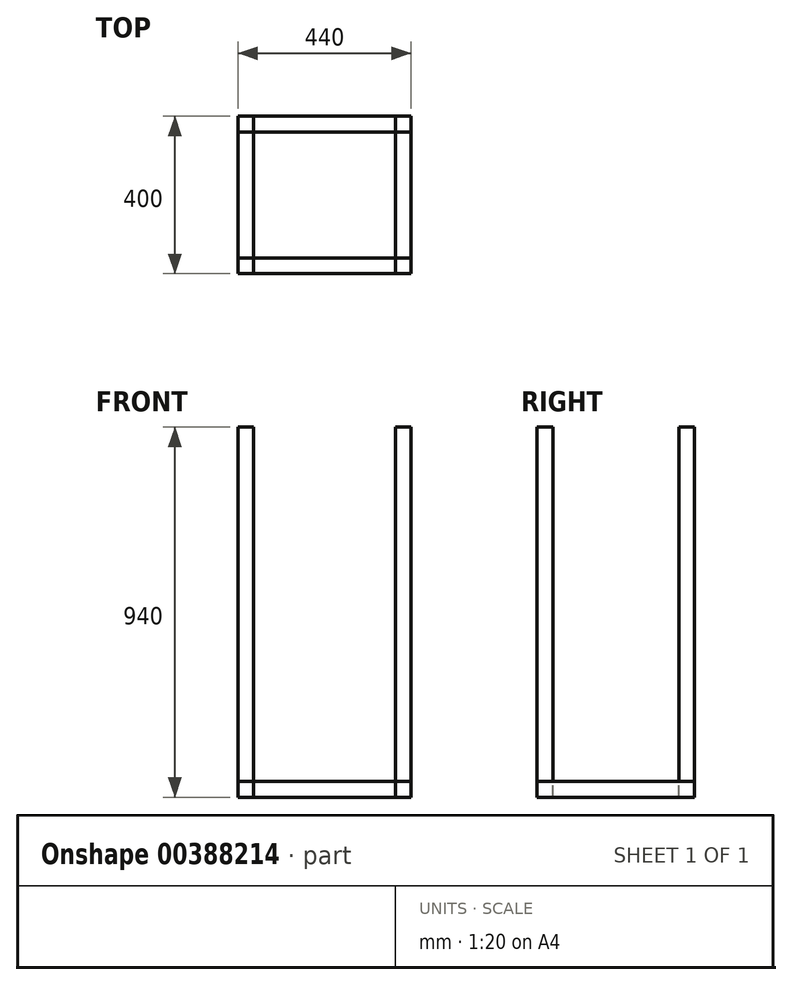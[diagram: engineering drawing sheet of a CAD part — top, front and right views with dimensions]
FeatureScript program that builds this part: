
annotation { "Feature Type Name" : "Feature", "Feature Type Description" : "" }
export const myFeature = defineFeature(function(context is Context, id is Id, definition is map)
    precondition{}
    {
        {
            var Q0;
            Q0=qCreatedBy(makeId("Top.planeOp"),FACE);
            var sketch = newSketch(context, id + "F0", { "sketchPlane" : qUnion([Q0])});
            skLineSegment(sketch, "E0.bottom", {"start": v(0, 0) * mm, "end": v(-40, 0) * mm});
            skLineSegment(sketch, "E0.top", {"start": v(0, 40) * mm, "end": v(-40, 40) * mm});
            skLineSegment(sketch, "E0.left", {"start": v(0, 0) * mm, "end": v(0, 40) * mm});
            skLineSegment(sketch, "E0.right", {"start": v(-40, 0) * mm, "end": v(-40, 40) * mm});
            skLineSegment(sketch, "E1.bottom", {"start": v(0, 360) * mm, "end": v(-40, 360) * mm});
            skLineSegment(sketch, "E1.top", {"start": v(0, 400) * mm, "end": v(-40, 400) * mm});
            skLineSegment(sketch, "E1.left", {"start": v(0, 360) * mm, "end": v(0, 400) * mm});
            skLineSegment(sketch, "E1.right", {"start": v(-40, 360) * mm, "end": v(-40, 400) * mm});
            skLineSegment(sketch, "E2.bottom", {"start": v(-440, 0) * mm, "end": v(-400, 0) * mm});
            skLineSegment(sketch, "E2.top", {"start": v(-440, 40) * mm, "end": v(-400, 40) * mm});
            skLineSegment(sketch, "E2.left", {"start": v(-440, 40) * mm, "end": v(-440, 0) * mm});
            skLineSegment(sketch, "E2.right", {"start": v(-400, 0) * mm, "end": v(-400, 40) * mm});
            skLineSegment(sketch, "E3.bottom", {"start": v(-440, 360) * mm, "end": v(-400, 360) * mm});
            skLineSegment(sketch, "E3.top", {"start": v(-440, 400) * mm, "end": v(-400, 400) * mm});
            skLineSegment(sketch, "E3.left", {"start": v(-440, 400) * mm, "end": v(-440, 360) * mm});
            skLineSegment(sketch, "E3.right", {"start": v(-400, 400) * mm, "end": v(-400, 360) * mm});
            skLineSegment(sketch, "E4", {"start": v(0, 40) * mm, "end": v(0, 360) * mm});
            skLineSegment(sketch, "E5", {"start": v(-40, 40) * mm, "end": v(-40, 360) * mm});
            skLineSegment(sketch, "E6", {"start": v(-440, 0) * mm, "end": v(-40, 0) * mm});
            skLineSegment(sketch, "E7", {"start": v(-440, 40) * mm, "end": v(-40, 40) * mm});
            skLineSegment(sketch, "E8", {"start": v(-440, 360) * mm, "end": v(-440, 40) * mm});
            skLineSegment(sketch, "E9", {"start": v(-400, 40) * mm, "end": v(-400, 360) * mm});
            skLineSegment(sketch, "E10", {"start": v(-40, 360) * mm, "end": v(-440, 360) * mm});
            skLineSegment(sketch, "E11", {"start": v(-440, 400) * mm, "end": v(-40, 400) * mm});
            skSolve(sketch);
        }
        {
            var Q0;
            Q0=makeQuery(id+"F0.imprint","IMPRINT",FACE,{"disambiguationData":[TD([[makeQuery(id+"F0.imprint","IMPRINT",EDGE,{"derivedFrom":sQuery(id+"F0.wireOp",EDGE,"E0.bottom")}),-1.0]])]});
            var Q1;
            Q1=makeQuery(id+"F0.imprint","IMPRINT",FACE,{"disambiguationData":[TD([[makeQuery(id+"F0.imprint","IMPRINT",EDGE,{"derivedFrom":sQuery(id+"F0.wireOp",EDGE,"E1.bottom")}),-1.0]])]});
            var Q2;
            {var subQ0=sQuery(id+"F0.wireOp",EDGE,"E2.left");Q2=makeQuery(id+"F0.imprint","IMPRINT",FACE,{"disambiguationData":[TD([[makeQuery(id+"F0.imprint","IMPRINT",EDGE,{"derivedFrom":subQ0}),1.0]])]});}
            var Q3;
            {var subQ0=sQuery(id+"F0.wireOp",EDGE,"E3.left");Q3=makeQuery(id+"F0.imprint","IMPRINT",FACE,{"disambiguationData":[TD([[makeQuery(id+"F0.imprint","IMPRINT",EDGE,{"derivedFrom":subQ0}),1.0]])]});}
            extrude(context, id + "F1", {"entities" : qUnion([Q0, Q1, Q2, Q3]), "depth" : 900 * mm});
        }
        {
            var Q0;
            {var subQ0=sQuery(id+"F0.wireOp",EDGE,"E2.left");Q0=makeQuery(id+"F0.imprint","IMPRINT",FACE,{"disambiguationData":[TD([[makeQuery(id+"F0.imprint","IMPRINT",EDGE,{"derivedFrom":subQ0}),1.0]])]});}
            var Q1;
            {var subQ0=sQuery(id+"F0.wireOp",EDGE,"E8");Q1=makeQuery(id+"F0.imprint","IMPRINT",FACE,{"disambiguationData":[TD([[makeQuery(id+"F0.imprint","IMPRINT",EDGE,{"derivedFrom":subQ0}),1.0]])]});}
            var Q2;
            {var subQ0=sQuery(id+"F0.wireOp",EDGE,"E3.left");Q2=makeQuery(id+"F0.imprint","IMPRINT",FACE,{"disambiguationData":[TD([[makeQuery(id+"F0.imprint","IMPRINT",EDGE,{"derivedFrom":subQ0}),1.0]])]});}
            var Q3;
            Q3=makeQuery(id+"F0.imprint","IMPRINT",FACE,{"disambiguationData":[TD([[makeQuery(id+"F0.imprint","IMPRINT",EDGE,{"derivedFrom":sQuery(id+"F0.wireOp",EDGE,"E0.bottom")}),-1.0]])]});
            var Q4;
            Q4=makeQuery(id+"F0.imprint","IMPRINT",FACE,{"disambiguationData":[TD([[makeQuery(id+"F0.imprint","IMPRINT",EDGE,{"derivedFrom":sQuery(id+"F0.wireOp",EDGE,"E0.top")}),-1.0]])]});
            var Q5;
            Q5=makeQuery(id+"F0.imprint","IMPRINT",FACE,{"disambiguationData":[TD([[makeQuery(id+"F0.imprint","IMPRINT",EDGE,{"derivedFrom":sQuery(id+"F0.wireOp",EDGE,"E1.bottom")}),-1.0]])]});
            extrude(context, id + "F2", {"entities" : qUnion([Q0, Q1, Q2, Q3, Q4, Q5]), "oppositeDirection" : true, "depth" : 40 * mm});
        }
        {
            var Q0;
            {var subQ0=sQuery(id+"F0.wireOp",EDGE,"E0.right");Q0=makeQuery(id+"F0.imprint","IMPRINT",FACE,{"disambiguationData":[TD([[makeQuery(id+"F0.imprint","IMPRINT",EDGE,{"derivedFrom":subQ0}),1.0]])]});}
            var Q1;
            {var subQ0=sQuery(id+"F0.wireOp",EDGE,"E1.right");Q1=makeQuery(id+"F0.imprint","IMPRINT",FACE,{"disambiguationData":[TD([[makeQuery(id+"F0.imprint","IMPRINT",EDGE,{"derivedFrom":subQ0}),1.0]])]});}
            extrude(context, id + "F3", {"entities" : qUnion([Q0, Q1]), "oppositeDirection" : true, "depth" : 40 * mm});
        }
    });
